FCSTD DOCUMENT  (FreeCAD 1.0R39109 (Git))
Label: BUZZER1
License: All rights reserved
objects: Sketcher::SketchObject×1, PartDesign::Body×1
note: 3 computed .brp shape members not serialized (recipe doc carries the construction recipe); baked Part::Feature solids carry a one-line shape summary decoded from their .brp

FEATURE [Sketcher::SketchObject] Sketch
  ArcFitTolerance = 1e-06
  AttachmentSupport = -> [XY_Plane]
  FullyConstrained = true
  MakeInternals = false
  MapMode = 5
  sketch-geometry (12):
    g0: ArcOfCircle CenterX=0 CenterY=0 CenterZ=0 NormalX=0 NormalY=0 NormalZ=1 AngleXU=0 Radius=4 StartAngle=5.56045 EndAngle=10.1475
    g1: LineSegment StartX=-3 StartY=-2.64575 StartZ=0 EndX=-3 EndY=-5.24575 EndZ=0
    g2: LineSegment StartX=-3 StartY=-5.24575 StartZ=0 EndX=3 EndY=-5.24575 EndZ=0
    g3: LineSegment StartX=3 StartY=-5.24575 StartZ=0 EndX=3 EndY=-2.64575 EndZ=0
    g4: LineSegment StartX=-5.25 StartY=0.8 StartZ=0 EndX=-5.25 EndY=-0.8 EndZ=0
    g5: LineSegment StartX=-5.25 StartY=-0.8 StartZ=0 EndX=-3.68 EndY=-0.8 EndZ=0
    g6: LineSegment StartX=-3.68 StartY=-0.8 StartZ=0 EndX=-3.68 EndY=0.8 EndZ=0
    g7: LineSegment StartX=-3.68 StartY=0.8 StartZ=0 EndX=-5.25 EndY=0.8 EndZ=0
    g8: LineSegment StartX=3.68 StartY=0.8 StartZ=0 EndX=3.68 EndY=-0.8 EndZ=0
    g9: LineSegment StartX=3.68 StartY=-0.8 StartZ=0 EndX=5.25 EndY=-0.8 EndZ=0
    g10: LineSegment StartX=5.25 StartY=-0.8 StartZ=0 EndX=5.25 EndY=0.8 EndZ=0
    g11: LineSegment StartX=5.25 StartY=0.8 StartZ=0 EndX=3.68 EndY=0.8 EndZ=0
  constraints (36):
    c: Coincident(g0,g-1)
    c: Diameter(g0) = 8
    c: Vertical(g1)
    c: Coincident(g1,g2)
    c: Horizontal(g2)
    c: Coincident(g2,g3)
    c: Coincident(g3,g0)
    c: Vertical(g3)
    c: Coincident(g1,g0)
    c: DistanceX(g2,g2) = 6
    c: DistanceX(g0,g0) = 3
    c: DistanceY(g3,g3) = 2.6
    c: Coincident(g4,g5)
    c: Coincident(g5,g6)
    c: Coincident(g6,g7)
    c: Coincident(g7,g4)
    c: Vertical(g4)
    c: Vertical(g6)
    c: Horizontal(g5)
    c: Horizontal(g7)
    c: Coincident(g8,g9)
    c: Coincident(g9,g10)
    c: Coincident(g10,g11)
    c: Coincident(g11,g8)
    c: Vertical(g8)
    c: Vertical(g10)
    c: Horizontal(g9)
    c: Horizontal(g11)
    c: DistanceX(g4,g9) = 10.5
    c: DistanceY(g10,g10) = 1.6
    c: Equal(g10,g4)
    c: DistanceY(g5,g0) = 0.8
    c: Equal(g11,g7)
    c: DistanceX(g7,g7) = 1.57
    c: DistanceX(g4,g0) = 5.25
    c: Horizontal(g8,g6)
FEATURE [PartDesign::Body] Body
  AllowCompound = false
  Group = -> [Sketch]
  Origin = -> Origin
